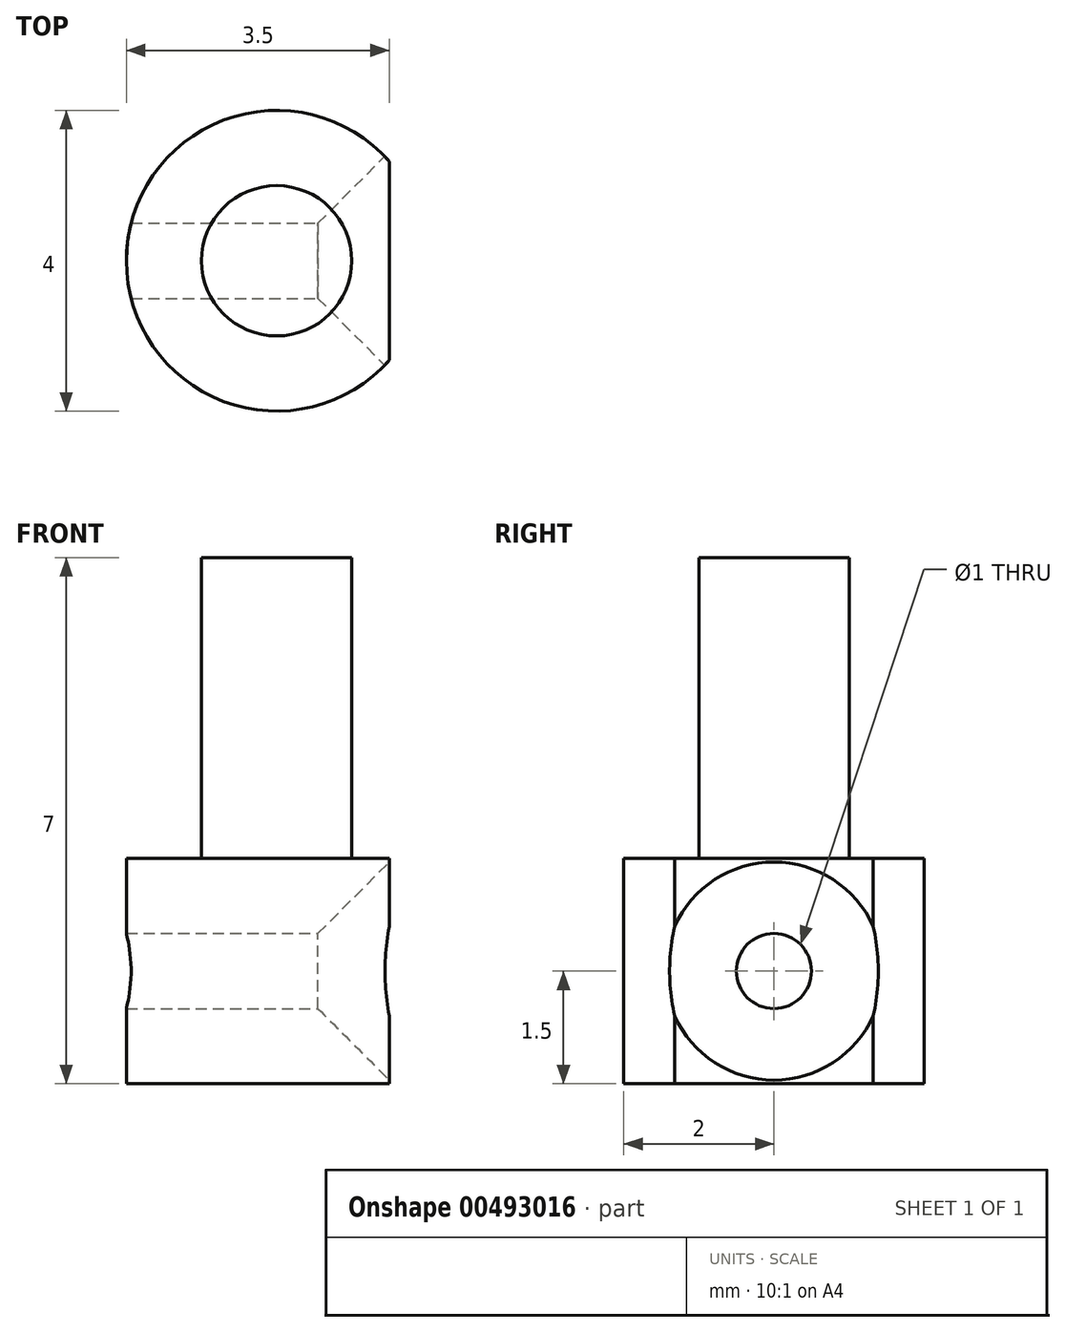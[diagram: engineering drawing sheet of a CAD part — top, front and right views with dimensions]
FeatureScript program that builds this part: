
annotation { "Feature Type Name" : "Feature", "Feature Type Description" : "" }
export const myFeature = defineFeature(function(context is Context, id is Id, definition is map)
    precondition{}
    {
        {
            var Q0;
            Q0=qCreatedBy(makeId("Top.planeOp"),FACE);
            var sketch = newSketch(context, id + "F0", { "sketchPlane" : qUnion([Q0])});
            skCircle(sketch, "E0", {"center": v(0, 0) * mm, "radius": 1 * mm});
            skSolve(sketch);
        }
        {
            var Q0;
            Q0 = qSketchRegion(id + "F0", true);
            extrude(context, id + "F1", {"entities" : qUnion([Q0]), "depth" : 4 * mm});
        }
        {
            var Q0;
            Q0=makeQuery(id+"F1.opExtrude","CAP_FACE",FACE,{"disambiguationData":[OSD([sQuery(id+"F0.wireOp",EDGE,"E0")])],"isStart":true});
            var sketch = newSketch(context, id + "F2", { "sketchPlane" : qUnion([Q0])});
            skCircle(sketch, "E1", {"center": v(0, 0) * mm, "radius": 2 * mm});
            skSolve(sketch);
        }
        {
            var Q0;
            Q0 = qSketchRegion(id + "F2", true);
            extrude(context, id + "F3", {"entities" : qUnion([Q0]), "operationType" : NewBodyOperationType.ADD, "depth" : 3 * mm});
        }
        {
            var Q0;
            Q0=qCreatedBy(makeId("Right.planeOp"),FACE);
            cPlane(context, id + "F4", {"entities" : qUnion([Q0]), "cplaneType" : CPlaneType.OFFSET, "offset" : 1.5 * mm, "width" : 150 * mm, "height" : 150 * mm});
        }
        {
            var Q0;
            Q0=qCreatedBy(id+"F4.planeOp",FACE);
            var sketch = newSketch(context, id + "F5", { "sketchPlane" : qUnion([Q0])});
            skPoint(sketch, "E2", {"position": v(0, -1.5) * mm});
            skSolve(sketch);
        }
        {
            var Q0;
            Q0=sQuery(id+"F5.wireOp",VERTEX,"E2");
            var Q1;
            Q1=makeQuery(id+"F1.opExtrude","SWEPT_BODY",BODY,{"disambiguationData":[OSD([sQuery(id+"F0.wireOp",EDGE,"E0")])]});
            hole(context, id + "F6", {"style" : HoleStyle.C_SINK, "endStyle" : HoleEndStyle.THROUGH, "holeDiameter" : 1 * mm, "cSinkDiameter" : 2.9 * mm, "cSinkAngle" : 90 * degree, "isTappedThrough" : true, "tappedDepth" : 12 * mm, "tapClearance" : 3, "locations" : qUnion([Q0]), "scope" : qUnion([Q1])});
        }
        {
            var Q0;
            Q0=qCreatedBy(makeId("Front.planeOp"),FACE);
            var sketch = newSketch(context, id + "F7", { "sketchPlane" : qUnion([Q0])});
            skLineSegment(sketch, "E3.bottom", {"start": v(1.5, 0.1) * mm, "end": v(5.24, 0.1) * mm});
            skLineSegment(sketch, "E3.top", {"start": v(1.5, -4.86) * mm, "end": v(5.24, -4.86) * mm});
            skLineSegment(sketch, "E3.left", {"start": v(1.5, 0.1) * mm, "end": v(1.5, -4.86) * mm});
            skLineSegment(sketch, "E3.right", {"start": v(5.24, 0.1) * mm, "end": v(5.24, -4.86) * mm});
            skSolve(sketch);
        }
        {
            var Q0;
            Q0 = qSketchRegion(id + "F7", true);
            extrude(context, id + "F8", {"entities" : qUnion([Q0]), "operationType" : NewBodyOperationType.REMOVE, "depth" : 25 * mm, "hasSecondDirection" : true, "secondDirectionOppositeDirection" : true, "secondDirectionDepth" : 25 * mm});
        }
    });
